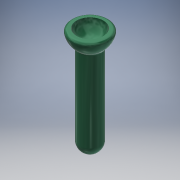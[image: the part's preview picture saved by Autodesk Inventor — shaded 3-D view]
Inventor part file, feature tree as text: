
AUTODESK INVENTOR PART (.ipt)
format: ipt  version: 2018 (Build 220112000, 112)  size: 147,968 bytes
history: native  units: mm
features: revolve x1, sketch x1
ambient origin geometry x8: Origin, YZ Plane, XZ Plane, XY Plane, X Axis, Y Axis, Z Axis, Center Point
bodies: Solid1 (feature_tree)
feature tree (2):
  revolve  "Revolution1"  [1 undecoded]
  sketch  "Sketch1"  dims[d0=20.0mm d1=5.0mm d2=7.0mm d3=2.0mm d4=2.0mm d5=0.25mm d6=0.25mm d7=1.0mm d8=1.0mm d9=90.0deg]
note: 1 required parameter value undecoded (feature->parameter linkage not recoverable at this tier; creation-order binding heuristic only, values carry confidence <= 0.55)
